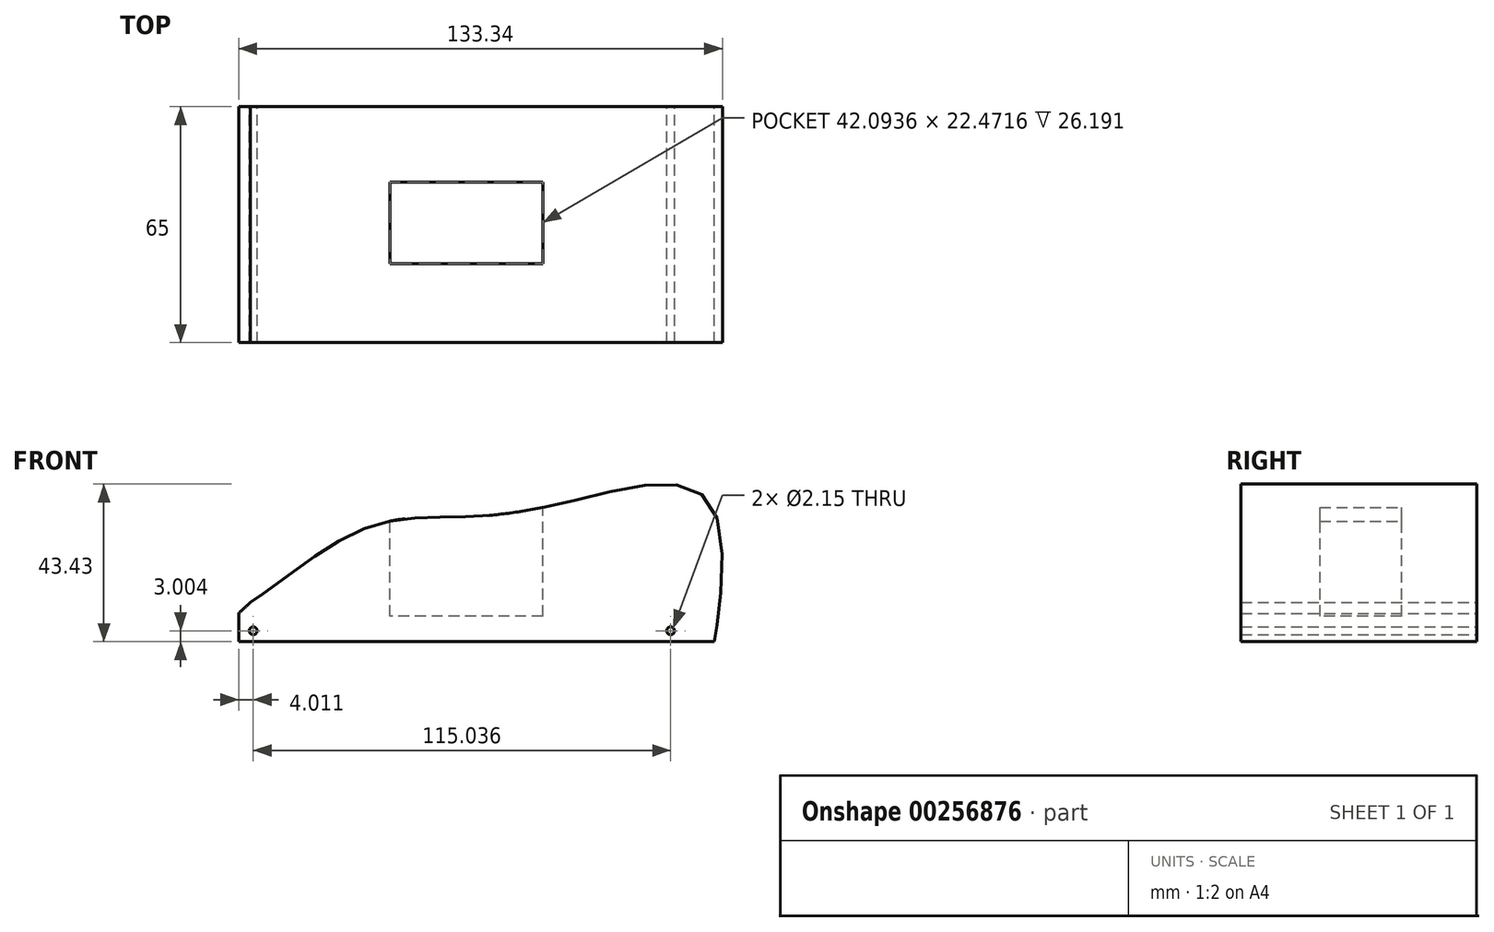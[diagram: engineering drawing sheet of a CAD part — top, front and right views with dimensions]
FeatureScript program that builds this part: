
annotation { "Feature Type Name" : "Feature", "Feature Type Description" : "" }
export const myFeature = defineFeature(function(context is Context, id is Id, definition is map)
    precondition{}
    {
        {
            var Q0;
            Q0=qCreatedBy(makeId("Front.planeOp"),FACE);
            var sketch = newSketch(context, id + "F0", { "sketchPlane" : qUnion([Q0])});
            skPoint(sketch, "E0.middle", {"position": v(0, 0) * mm});
            skLineSegment(sketch, "E1", {"start": v(57.35, 18.73) * mm, "end": v(57.35, 18.73) * mm});
            skLineSegment(sketch, "E2", {"start": v(57.35, 19.7) * mm, "end": v(57.35, 18.73) * mm});
            skFitSpline(sketch, "E3", {"points": [v(-59.5, 14.3) * mm, v(-50.5, 20.73) * mm, v(-25.98, 35.39) * mm, v(0, 37.86) * mm, v(31.67, 42.81) * mm, v(67.56, 41.08) * mm, v(68.3, 3.46) * mm, v(68.3, 3.22) * mm], "startDerivative": vector(82.7, 57.38) * mm, "endDerivative": vector(4.53, -5.63) * mm});
            skFitSpline(sketch, "E4", {"points": [v(-59.5, 14.3) * mm, v(-65.82, 7.92) * mm, v(-64.34, 8.41) * mm], "startDerivative": vector(-13.9, -12.81) * mm, "endDerivative": vector(7.1, 3.26) * mm});
            skLineSegment(sketch, "E5", {"start": v(68.3, 3.46) * mm, "end": v(-62.77, 3.46) * mm});
            skLineSegment(sketch, "E6", {"start": v(68.3, 3.46) * mm, "end": v(56.28, 3.46) * mm});
            skLineSegment(sketch, "E7", {"start": v(-67.02, 3.46) * mm, "end": v(-66.8, 3.46) * mm});
            skLineSegment(sketch, "E8", {"start": v(56.28, 3.46) * mm, "end": v(56.28, 6.46) * mm});
            skCircle(sketch, "E9", {"center": v(56.28, 6.46) * mm, "radius": 1.07 * mm});
            skPoint(sketch, "E10", {"position": v(-46.23, 7.35) * mm});
            skCircle(sketch, "E11", {"center": v(-58.76, 6.46) * mm, "radius": 1.07 * mm});
            skLineSegment(sketch, "E12", {"start": v(-62.77, 11.28) * mm, "end": v(-62.77, 3.46) * mm});
            skLineSegment(sketch, "E13.trimOffspring", {"start": v(-66.8, 3.46) * mm, "end": v(-67.02, 3.46) * mm});
            skSolve(sketch);
        }
        {
            var Q0;
            Q0 = qSketchRegion(id + "F0", true);
            extrude(context, id + "F1", {"entities" : qUnion([Q0]), "depth" : 40 * mm});
        }
        {
            var Q0;
            {var subQ0=sQuery(id+"F0.wireOp",EDGE,"ZruWdidO-0ean-B9Hg-MqqZ-eG3lBj00Jdhw");Q0=makeQuery(id+"F0.imprint","IMPRINT",FACE,{"disambiguationData":[TD([[makeQuery(id+"F0.imprint","IMPRINT",EDGE,{"derivedFrom":subQ0}),-1.0]])]});}
            var Q1;
            Q1=makeQuery(id+"F1.opExtrude","CAP_FACE",FACE,{"disambiguationData":[OSD([sQuery(id+"F0.wireOp",EDGE,"E3"),sQuery(id+"F0.wireOp",EDGE,"E4"),sQuery(id+"F0.wireOp",EDGE,"ZruWdidO-0ean-B9Hg-MqqZ-eG3lBj00Jdhw"),sQuery(id+"F0.wireOp",EDGE,"E5"),sQuery(id+"F0.wireOp",EDGE,"4U62VM8j-nFJD-diuK-fIj4-3ZPWIkv4szRv"),sQuery(id+"F0.wireOp",EDGE,"E6"),sQuery(id+"F0.wireOp",EDGE,"E7"),sQuery(id+"F0.wireOp",EDGE,"E9")])],"isStart":false});
            extrude(context, id + "F2", {"entities" : qUnion([Q0, Q1]), "operationType" : NewBodyOperationType.ADD, "depth" : 25 * mm});
        }
        {
            var Q0;
            Q0=makeQuery(id+"F0.imprint","IMPRINT",FACE,{"disambiguationData":[TD([[makeQuery(id+"F0.imprint","IMPRINT",EDGE,{"derivedFrom":sQuery(id+"F0.wireOp",EDGE,"E11")}),1.0]])]});
            extrude(context, id + "F3", {"entities" : qUnion([Q0]), "operationType" : NewBodyOperationType.REMOVE, "endBound" : BoundingType.THROUGH_ALL, "depth" : 25 * mm});
        }
        {
            var Q0;
            Q0=qCreatedBy(makeId("Top.planeOp"),FACE);
            cPlane(context, id + "F4", {"entities" : qUnion([Q0]), "cplaneType" : CPlaneType.OFFSET, "offset" : 50.9 * mm, "width" : 150 * mm, "height" : 150 * mm});
        }
        {
            var Q0;
            Q0=qCreatedBy(id+"F4.planeOp",FACE);
            var sketch = newSketch(context, id + "F5", { "sketchPlane" : qUnion([Q0])});
            skPoint(sketch, "E14", {"position": v(0, -32) * mm});
            skLineSegment(sketch, "E15.bottom", {"start": v(21.05, -20.76) * mm, "end": v(-21.05, -20.76) * mm});
            skLineSegment(sketch, "E15.top", {"start": v(21.05, -43.24) * mm, "end": v(-21.05, -43.24) * mm});
            skLineSegment(sketch, "E15.left", {"start": v(21.05, -20.76) * mm, "end": v(21.05, -43.24) * mm});
            skLineSegment(sketch, "E15.right", {"start": v(-21.05, -20.76) * mm, "end": v(-21.05, -43.24) * mm});
            skSolve(sketch);
        }
        {
            var Q0;
            Q0=makeQuery(id+"F5.imprint","IMPRINT",FACE,{"disambiguationData":[TD([[makeQuery(id+"F5.imprint","IMPRINT",EDGE,{"derivedFrom":sQuery(id+"F5.wireOp",EDGE,"E15.bottom")}),1.0]])]});
            extrude(context, id + "F6", {"entities" : qUnion([Q0]), "operationType" : NewBodyOperationType.REMOVE, "oppositeDirection" : true, "depth" : 40.4 * mm});
        }
    });
